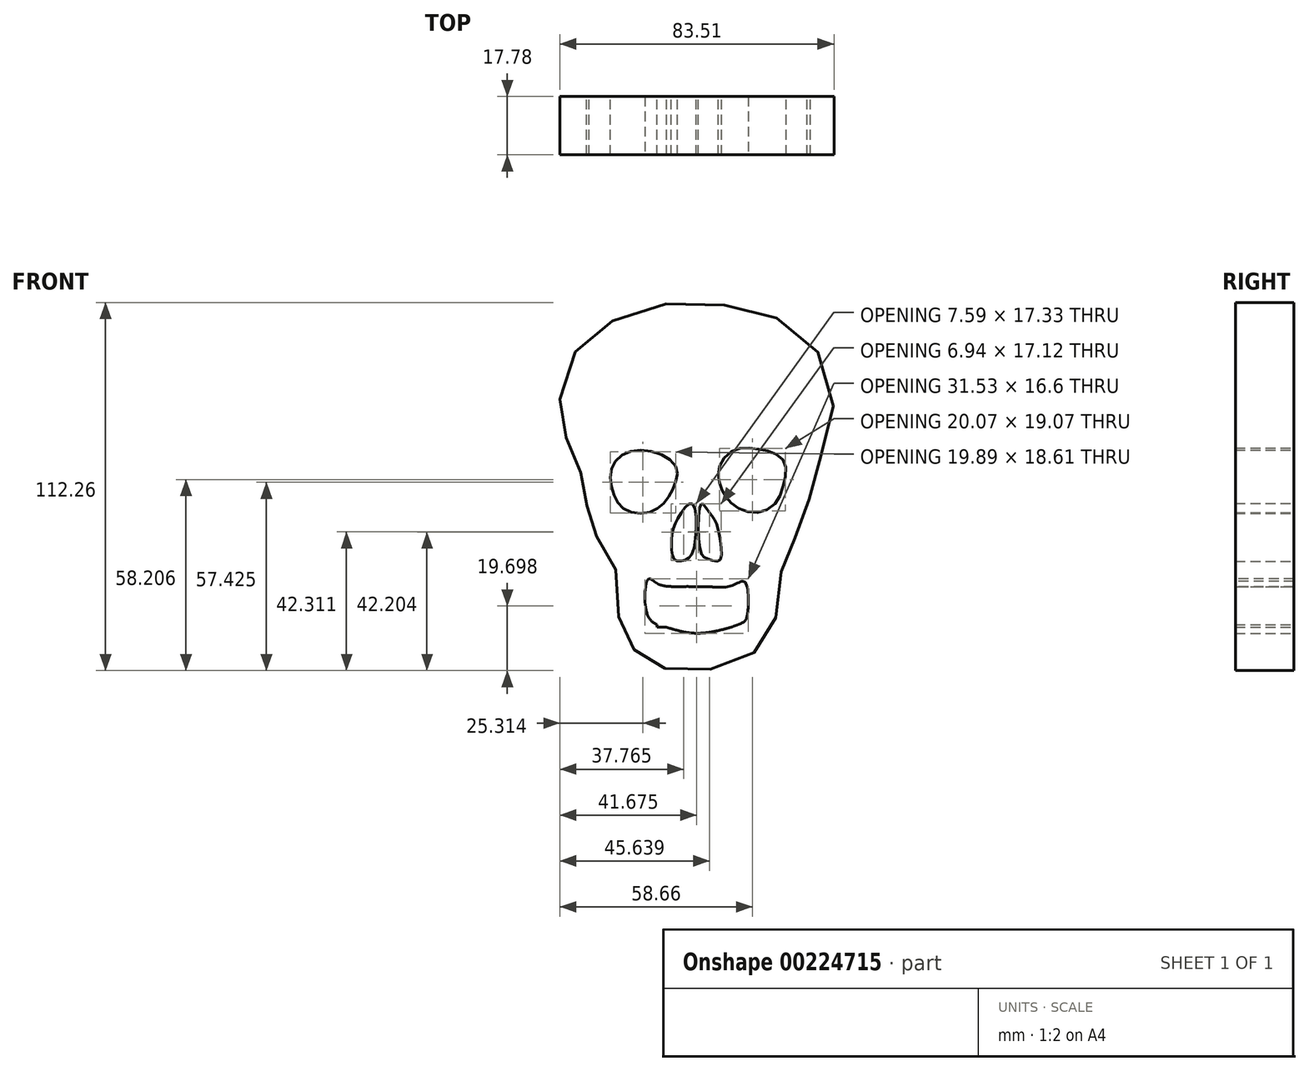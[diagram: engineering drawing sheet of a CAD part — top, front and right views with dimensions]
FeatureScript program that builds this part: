
annotation { "Feature Type Name" : "Feature", "Feature Type Description" : "" }
export const myFeature = defineFeature(function(context is Context, id is Id, definition is map)
    precondition{}
    {
        {
            var Q0;
            Q0=qCreatedBy(makeId("Front.planeOp"),FACE);
            var sketch = newSketch(context, id + "F0", { "sketchPlane" : qUnion([Q0])});
            skFitSpline(sketch, "E0", {"points": [v(-20.92, -71.26) * mm, v(-26.07, -68.84) * mm, v(-30.91, -64.9) * mm, v(-33.79, -60.52) * mm, v(-35.3, -52.5) * mm, v(-35.75, -42.36) * mm, v(-38.02, -34.18) * mm, v(-42.26, -30.4) * mm, v(-43.47, -26.31) * mm, v(-44.68, -21.17) * mm, v(-44.23, -13.75) * mm, v(-47.4, -10.88) * mm, v(-50.28, -4.67) * mm, v(-51.5, 2.44) * mm, v(-52.85, 8.8) * mm, v(-50.94, 18.9) * mm, v(-45.6, 28.81) * mm, v(-36.64, 34.72) * mm, v(-23.1, 39.49) * mm, v(-7.66, 40.06) * mm, v(6.45, 37.77) * mm, v(17.7, 33.2) * mm, v(27.04, 23.1) * mm, v(30.47, 9.17) * mm, v(28.76, -3.6) * mm, v(22.66, -12.57) * mm, v(23.42, -22.48) * mm, v(20.37, -30.1) * mm, v(15.6, -34.68) * mm, v(14.65, -41.36) * mm, v(13.31, -50.5) * mm, v(11.98, -60.23) * mm, v(7.02, -65.95) * mm, v(-2.32, -70.34) * mm, v(-11.28, -71.86) * mm, v(-20.92, -71.26) * mm]});
            skFitSpline(sketch, "E1", {"points": [v(-17.61, -9.63) * mm, v(-17.7, -14.88) * mm, v(-20.75, -20.41) * mm, v(-25.73, -23.64) * mm, v(-33.1, -22.81) * mm, v(-36.52, -18.02) * mm, v(-37.35, -11.1) * mm, v(-33.2, -5.75) * mm, v(-24.25, -5.3) * mm, v(-17.61, -9.63) * mm]});
            skFitSpline(sketch, "E2", {"points": [v(-4.24, -9.63) * mm, v(-4.24, -14.42) * mm, v(-2.77, -18.39) * mm, v(0.92, -21.98) * mm, v(7, -23.73) * mm, v(12.9, -20.7) * mm, v(15.4, -14.79) * mm, v(15.68, -8.52) * mm, v(11.8, -5.38) * mm, v(5.72, -4.19) * mm, v(0, -4.74) * mm, v(-4.24, -9.63) * mm]});
            skFitSpline(sketch, "E3", {"points": [v(-12.45, -21.06) * mm, v(-12.26, -35.45) * mm, v(-14.85, -38.21) * mm, v(-17.61, -38.3) * mm, v(-18.81, -34.98) * mm, v(-18.54, -29.54) * mm, v(-15.95, -23.83) * mm, v(-12.45, -21.06) * mm]});
            skFitSpline(sketch, "E4", {"points": [v(-9.87, -21.06) * mm, v(-9.96, -35.63) * mm, v(-7.84, -37.84) * mm, v(-4.24, -38.3) * mm, v(-4.24, -31.02) * mm, v(-5.63, -26.13) * mm, v(-8.02, -22.72) * mm, v(-9.87, -21.06) * mm]});
            skFitSpline(sketch, "E5", {"points": [v(-25.88, -43.99) * mm, v(-26.08, -55.14) * mm, v(-20.42, -58.73) * mm, v(-10.47, -60.52) * mm, v(2.1, -57.62) * mm, v(4.18, -55.14) * mm, v(3.48, -44.91) * mm, v(0, -45.88) * mm, v(-5.91, -46.43) * mm, v(-15.72, -46.3) * mm, v(-23.32, -45.33) * mm, v(-25.88, -43.99) * mm]});
            skLineSegment(sketch, "E6", {"start": v(-23.32, -58.73) * mm, "end": v(-20.42, -58.73) * mm});
            skLineSegment(sketch, "E7", {"start": v(-18.7, -58.73) * mm, "end": v(-14.03, -60.3) * mm});
            skLineSegment(sketch, "E8", {"start": v(-2.33, -59.15) * mm, "end": v(2.1, -57.62) * mm});
            skLineSegment(sketch, "E9", {"start": v(-23.32, -45.33) * mm, "end": v(-23.32, -58.73) * mm});
            skLineSegment(sketch, "E10", {"start": v(-20.42, -46.18) * mm, "end": v(-20.42, -58.73) * mm});
            skLineSegment(sketch, "E11", {"start": v(-15.72, -46.3) * mm, "end": v(-15.72, -59.98) * mm});
            skLineSegment(sketch, "E12", {"start": v(-10.77, -46.3) * mm, "end": v(-10.47, -60.52) * mm});
            skLineSegment(sketch, "E13", {"start": v(-5.91, -46.43) * mm, "end": v(-5.91, -59.99) * mm});
            skLineSegment(sketch, "E14", {"start": v(-2.33, -46.43) * mm, "end": v(-2.33, -59.15) * mm});
            skLineSegment(sketch, "E15", {"start": v(2.1, -57.62) * mm, "end": v(2.1, -44.91) * mm});
            skLineSegment(sketch, "E16", {"start": v(-26.76, -52.54) * mm, "end": v(4.5, -52.54) * mm});
            skSolve(sketch);
        }
        {
            var Q0;
            Q0=makeQuery(id+"F0.imprint","IMPRINT",FACE,{"disambiguationData":[TD([[makeQuery(id+"F0.imprint","IMPRINT",EDGE,{"derivedFrom":sQuery(id+"F0.wireOp",EDGE,"E0")}),-1.0]])]});
            var Q1;
            Q1=sQuery(id+"F0.wireOp",EDGE,"E0");
            extrude(context, id + "F1", {"entities" : qUnion([Q0]), "surfaceEntities" : qUnion([Q1]), "depth" : 17.78 * mm});
        }
        {
            var Q0;
            Q0=makeQuery(id+"F0.imprint","IMPRINT",FACE,{"disambiguationData":[TD([[makeQuery(id+"F0.imprint","IMPRINT",EDGE,{"derivedFrom":sQuery(id+"F0.wireOp",EDGE,"E1")}),-1.0]])]});
            var Q1;
            Q1=sQuery(id+"F0.wireOp",EDGE,"E1");
            var Q2;
            Q2=sQuery(id+"F0.wireOp",EDGE,"E2");
            var Q3;
            Q3=sQuery(id+"F0.wireOp",EDGE,"E4");
            var Q4;
            Q4=sQuery(id+"F0.wireOp",EDGE,"E3");
            extrude(context, id + "F2", {"entities" : qUnion([Q0]), "bodyType" : ToolBodyType.SURFACE, "surfaceEntities" : qUnion([Q1, Q2, Q3, Q4]), "depth" : 17.78 * mm});
        }
        {
            var Q0;
            Q0=makeQuery(id+"F0.imprint","IMPRINT",FACE,{"disambiguationData":[TD([[makeQuery(id+"F0.imprint","IMPRINT",EDGE,{"derivedFrom":sQuery(id+"F0.wireOp",EDGE,"E2")}),1.0]])]});
            var Q1;
            Q1=sQuery(id+"F0.wireOp",EDGE,"E2");
            extrude(context, id + "F3", {"entities" : qUnion([Q0]), "bodyType" : ToolBodyType.SURFACE, "surfaceEntities" : qUnion([Q1]), "depth" : 17.78 * mm});
        }
        {
            var Q0;
            Q0=makeQuery(id+"F0.imprint","IMPRINT",FACE,{"disambiguationData":[TD([[makeQuery(id+"F0.imprint","IMPRINT",EDGE,{"derivedFrom":sQuery(id+"F0.wireOp",EDGE,"E3")}),-1.0]])]});
            var Q1;
            Q1=sQuery(id+"F0.wireOp",EDGE,"E3");
            extrude(context, id + "F4", {"entities" : qUnion([Q0]), "bodyType" : ToolBodyType.SURFACE, "surfaceEntities" : qUnion([Q1]), "depth" : 17.78 * mm});
        }
        {
            var Q0;
            Q0=makeQuery(id+"F0.imprint","IMPRINT",FACE,{"disambiguationData":[TD([[makeQuery(id+"F0.imprint","IMPRINT",EDGE,{"derivedFrom":sQuery(id+"F0.wireOp",EDGE,"E4")}),1.0]])]});
            var Q1;
            Q1=sQuery(id+"F0.wireOp",EDGE,"E4");
            extrude(context, id + "F5", {"entities" : qUnion([Q0]), "bodyType" : ToolBodyType.SURFACE, "surfaceEntities" : qUnion([Q1]), "depth" : 17.78 * mm});
        }
        {
            var Q0;
            Q0=makeQuery(id+"F0.imprint","IMPRINT",FACE,{"disambiguationData":[TD([[makeQuery(id+"F0.imprint","IMPRINT",EDGE,{"derivedFrom":sQuery(id+"F0.wireOp",EDGE,"E5")}),1.0]])]});
            var Q1;
            Q1=sQuery(id+"F0.wireOp",EDGE,"E5");
            extrude(context, id + "F6", {"entities" : qUnion([Q0]), "bodyType" : ToolBodyType.SURFACE, "surfaceEntities" : qUnion([Q1]), "depth" : 17.78 * mm});
        }
    });
